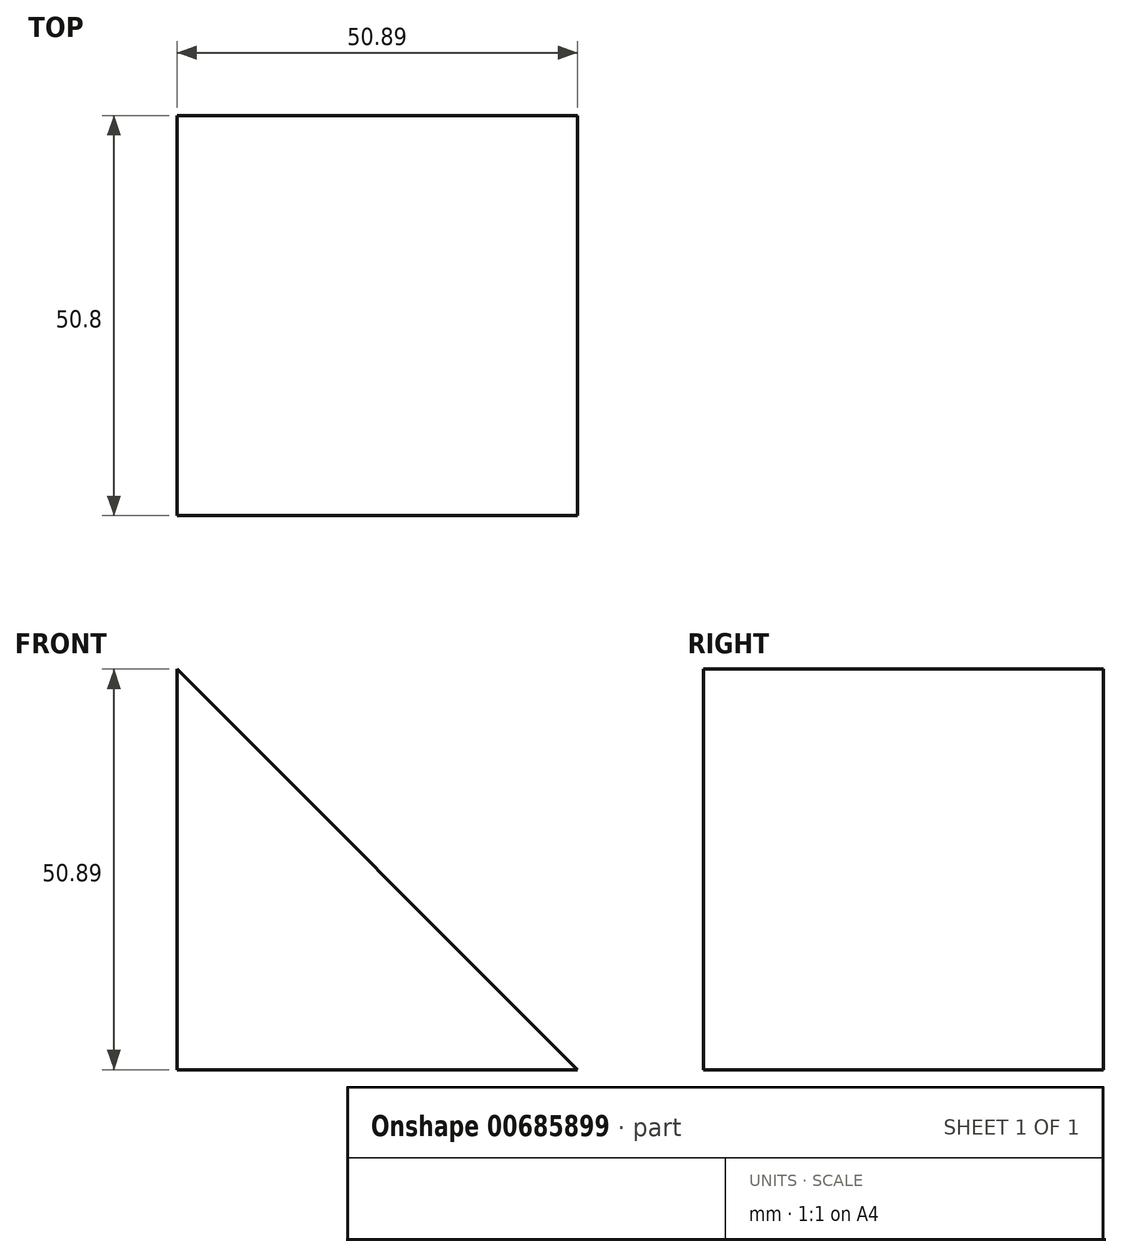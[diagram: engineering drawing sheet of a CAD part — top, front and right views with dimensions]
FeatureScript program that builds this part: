
annotation { "Feature Type Name" : "Feature", "Feature Type Description" : "" }
export const myFeature = defineFeature(function(context is Context, id is Id, definition is map)
    precondition{}
    {
        {
            var Q0;
            Q0=qCreatedBy(makeId("Front.planeOp"),FACE);
            var sketch = newSketch(context, id + "F0", { "sketchPlane" : qUnion([Q0])});
            skLineSegment(sketch, "E0", {"start": v(0, 0) * mm, "end": v(50.89, 0) * mm});
            skLineSegment(sketch, "E1", {"start": v(0, 0) * mm, "end": v(0, 50.89) * mm});
            skLineSegment(sketch, "E2", {"start": v(0, 50.89) * mm, "end": v(50.89, 0) * mm});
            skSolve(sketch);
        }
        {
            var Q0;
            Q0 = qSketchRegion(id + "F0", true);
            extrude(context, id + "F1", {"entities" : qUnion([Q0]), "depth" : 50.8 * mm, "offsetDistance" : 25.4 * mm});
        }
    });
